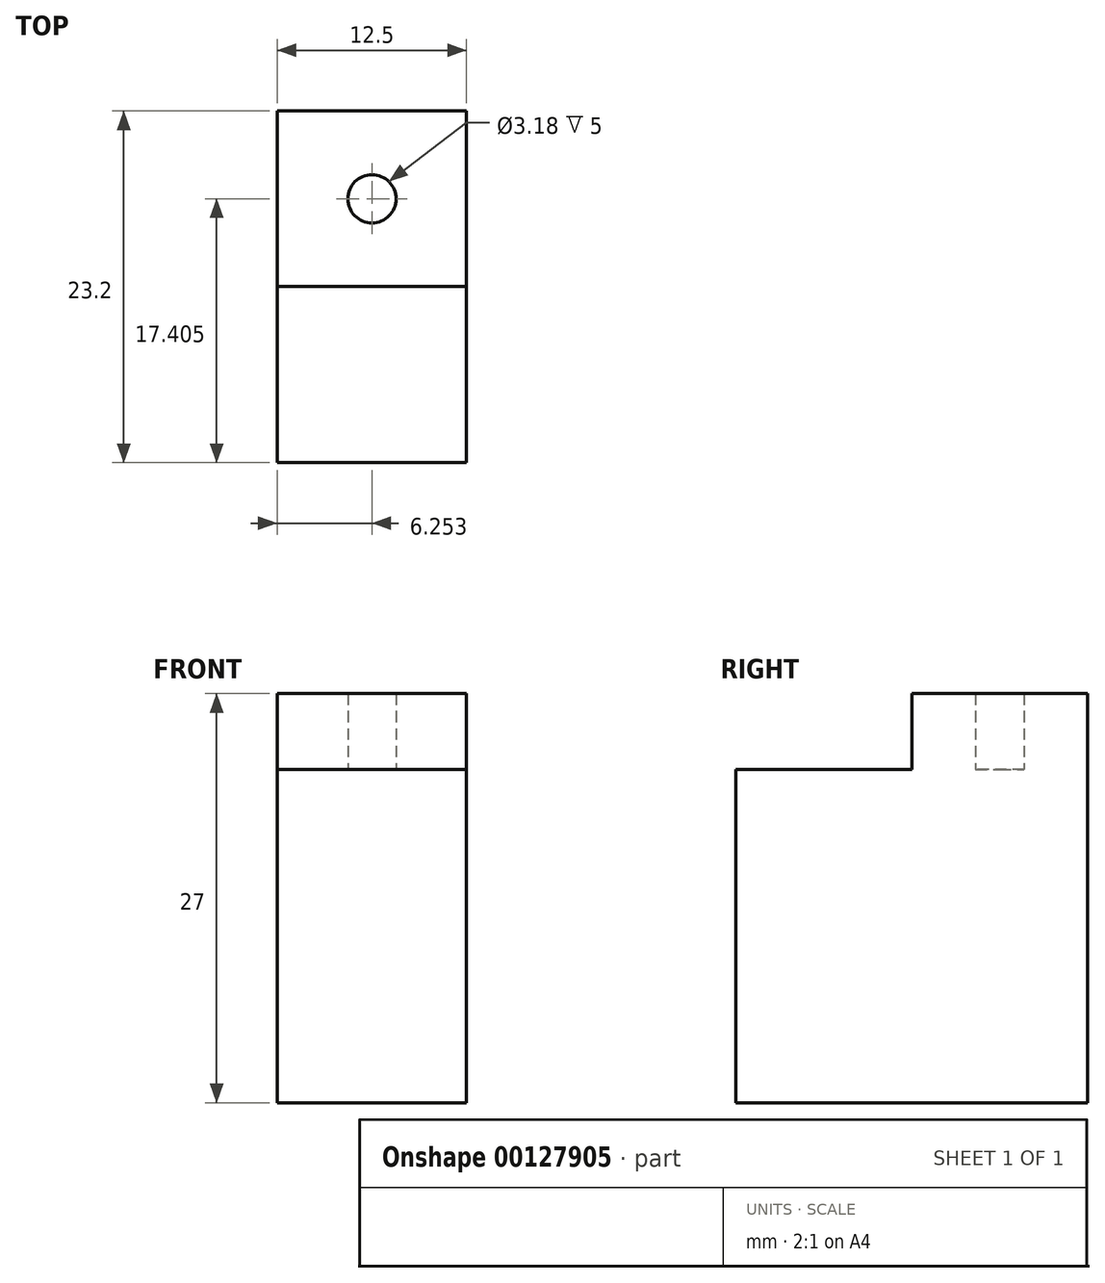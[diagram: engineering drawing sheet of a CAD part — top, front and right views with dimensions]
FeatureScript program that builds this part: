
annotation { "Feature Type Name" : "Feature", "Feature Type Description" : "" }
export const myFeature = defineFeature(function(context is Context, id is Id, definition is map)
    precondition{}
    {
        {
            var Q0;
            Q0=qCreatedBy(makeId("Top.planeOp"),FACE);
            var sketch = newSketch(context, id + "F0", { "sketchPlane" : qUnion([Q0])});
            skLineSegment(sketch, "E0.bottom", {"start": v(-13.6, 25.08) * mm, "end": v(-1.1, 25.08) * mm});
            skLineSegment(sketch, "E0.top", {"start": v(-13.6, 1.88) * mm, "end": v(-1.1, 1.88) * mm});
            skLineSegment(sketch, "E0.left", {"start": v(-13.6, 25.08) * mm, "end": v(-13.6, 1.88) * mm});
            skLineSegment(sketch, "E0.right", {"start": v(-1.1, 25.08) * mm, "end": v(-1.1, 1.88) * mm});
            skSolve(sketch);
        }
        {
            var Q0;
            Q0=makeQuery(id+"F0.imprint","IMPRINT",FACE,{"disambiguationData":[TD([[makeQuery(id+"F0.imprint","IMPRINT",EDGE,{"derivedFrom":sQuery(id+"F0.wireOp",EDGE,"E0.bottom")}),-1.0]])]});
            extrude(context, id + "F1", {"entities" : qUnion([Q0]), "depth" : 22 * mm});
        }
        {
            var Q0;
            Q0=makeQuery(id+"F1.opExtrude","CAP_FACE",FACE,{"disambiguationData":[OSD([sQuery(id+"F0.wireOp",EDGE,"E0.bottom"),sQuery(id+"F0.wireOp",EDGE,"E0.top"),sQuery(id+"F0.wireOp",EDGE,"E0.left"),sQuery(id+"F0.wireOp",EDGE,"E0.right")])],"isStart":false});
            var sketch = newSketch(context, id + "F2", { "sketchPlane" : qUnion([Q0])});
            skLineSegment(sketch, "E1", {"start": v(-13.6, 13.48) * mm, "end": v(-1.1, 13.48) * mm});
            skLineSegment(sketch, "E2", {"start": v(-13.6, 13.48) * mm, "end": v(-13.6, 25.08) * mm});
            skLineSegment(sketch, "E3", {"start": v(-13.6, 19.28) * mm, "end": v(-1.1, 19.28) * mm});
            skCircle(sketch, "E4", {"center": v(-7.35, 19.28) * mm, "radius": 1.6 * mm});
            skSolve(sketch);
        }
        {
            var Q0;
            {var subQ0=sQuery(id+"F2.wireOp",EDGE,"E4");var subQ1=sQuery(id+"F2.wireOp",EDGE,"E3");var subQ2=makeQuery(id+"F2.imprint","INTERSECT",VERTEX,{"disambiguationData":[OD(0.0)],"derivedFrom":[subQ1,subQ0]});Q0=makeQuery(id+"F2.imprint","IMPRINT",FACE,{"disambiguationData":[TD([[makeQuery(id+"F2.imprint","IMPRINT",EDGE,{"disambiguationData":[TD([[subQ2,-1.0]])],"derivedFrom":subQ1}),1.0]])]});}
            var Q1;
            {var subQ0=sQuery(id+"F2.wireOp",EDGE,"E4");var subQ1=sQuery(id+"F2.wireOp",EDGE,"E3");var subQ2=makeQuery(id+"F2.imprint","INTERSECT",VERTEX,{"disambiguationData":[OD(0.0)],"derivedFrom":[subQ1,subQ0]});Q1=makeQuery(id+"F2.imprint","IMPRINT",FACE,{"disambiguationData":[TD([[makeQuery(id+"F2.imprint","IMPRINT",EDGE,{"disambiguationData":[TD([[subQ2,-1.0]])],"derivedFrom":subQ1}),-1.0]])]});}
            extrude(context, id + "F3", {"entities" : qUnion([Q0, Q1]), "operationType" : NewBodyOperationType.ADD, "depth" : 5 * mm});
        }
    });
